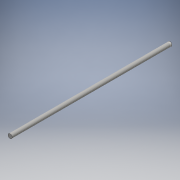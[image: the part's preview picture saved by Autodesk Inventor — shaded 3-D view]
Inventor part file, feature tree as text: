
AUTODESK INVENTOR PART (.ipt)
format: ipt  version: 2016 (Build 200138000, 138)  size: 89,600 bytes
history: native  units: mm
features: extrude x1, thread x1, sketch x1
ambient origin geometry x8: Origin, YZ Plane, XZ Plane, XY Plane, X Axis, Y Axis, Z Axis, Center Point
bodies: Solid1 (feature_tree)
feature tree (3):
  extrude  "Extrusion1"  Depth=530.0mm TaperAngle=0.0deg
  thread  "Thread1"  [1 undecoded]
  sketch  "Sketch1"  dims[d0=14.0mm d1=530.0mm d2=0.0mm d3=530.0mm d4=5.0mm]
note: 1 required parameter value undecoded (feature->parameter linkage not recoverable at this tier; creation-order binding heuristic only, values carry confidence <= 0.55)
